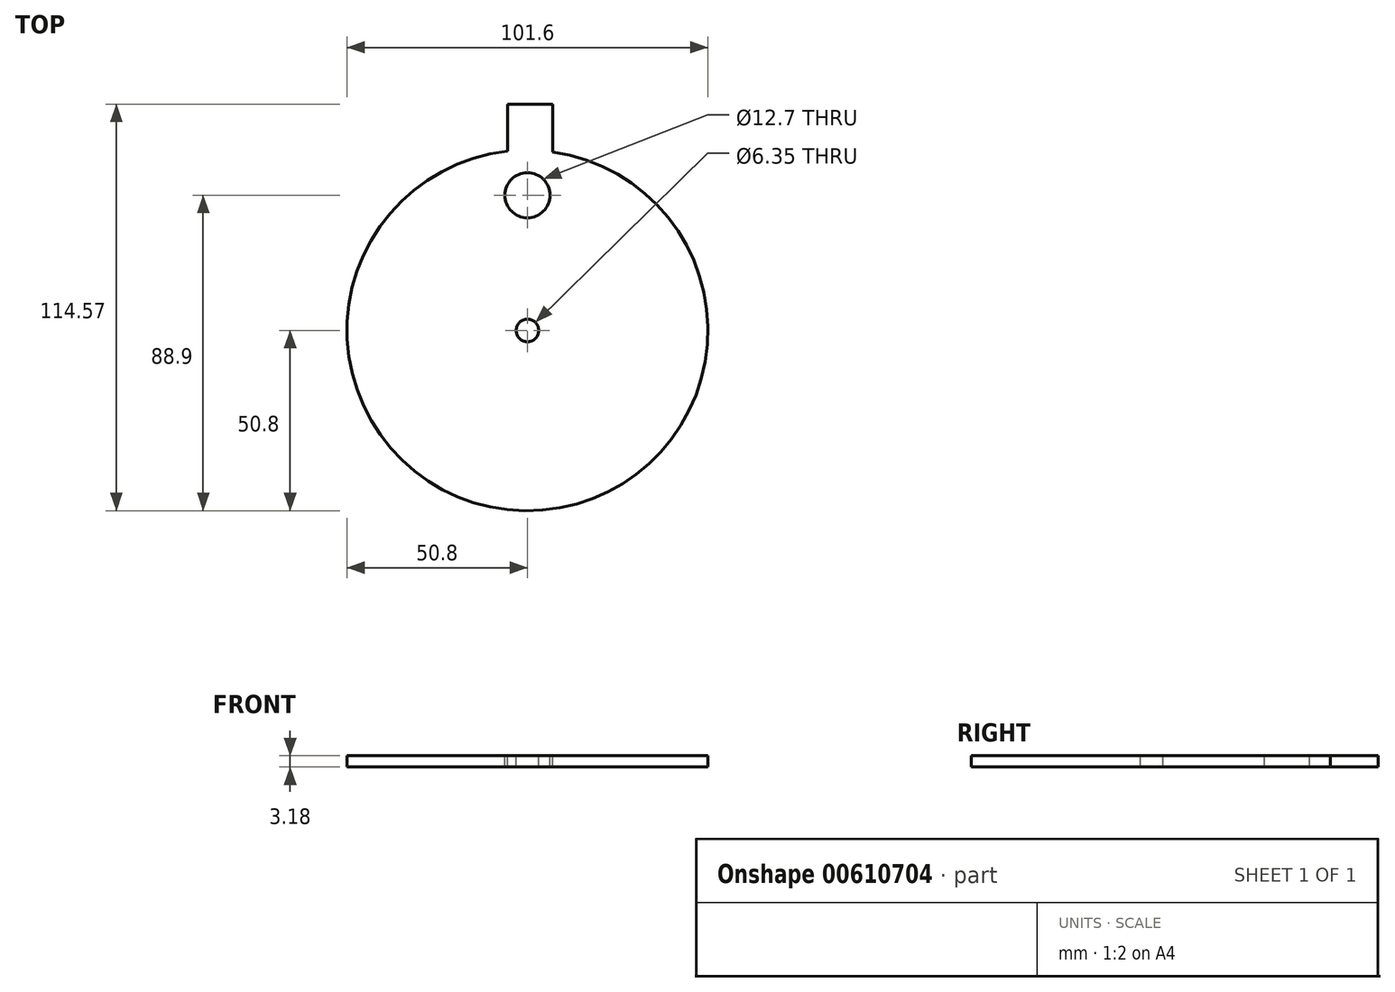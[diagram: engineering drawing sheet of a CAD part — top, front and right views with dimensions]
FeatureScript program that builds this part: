
annotation { "Feature Type Name" : "Feature", "Feature Type Description" : "" }
export const myFeature = defineFeature(function(context is Context, id is Id, definition is map)
    precondition{}
    {
        {
            var Q0;
            Q0=qCreatedBy(makeId("Top.planeOp"),FACE);
            var sketch = newSketch(context, id + "F0", { "sketchPlane" : qUnion([Q0])});
            skCircle(sketch, "E0", {"center": v(0, 0) * mm, "radius": 50.8 * mm});
            skSolve(sketch);
        }
        {
            var Q0;
            Q0=makeQuery(id+"F0.imprint","IMPRINT",FACE,{"disambiguationData":[TD([[makeQuery(id+"F0.imprint","IMPRINT",EDGE,{"derivedFrom":sQuery(id+"F0.wireOp",EDGE,"E0")}),1.0]])]});
            extrude(context, id + "F1", {"entities" : qUnion([Q0]), "depth" : 3.17 * mm, "offsetDistance" : 25.4 * mm});
        }
        {
            var Q0;
            Q0=makeQuery(id+"F1.opExtrude","CAP_FACE",FACE,{"disambiguationData":[OSD([sQuery(id+"F0.wireOp",EDGE,"E0")])],"isStart":false});
            var sketch = newSketch(context, id + "F2", { "sketchPlane" : qUnion([Q0])});
            skCircle(sketch, "E1", {"center": v(0, 38.1) * mm, "radius": 6.35 * mm});
            skSolve(sketch);
        }
        {
            var Q0;
            Q0=makeQuery(id+"F2.imprint","IMPRINT",FACE,{"disambiguationData":[TD([[makeQuery(id+"F2.imprint","IMPRINT",EDGE,{"derivedFrom":sQuery(id+"F2.wireOp",EDGE,"E1")}),1.0]])]});
            extrude(context, id + "F3", {"entities" : qUnion([Q0]), "operationType" : NewBodyOperationType.REMOVE, "depth" : -3.17 * mm, "offsetDistance" : 25.4 * mm});
        }
        {
            var Q0;
            Q0=makeQuery(id+"F2.imprint","IMPRINT",FACE,{"disambiguationData":[TD([[makeQuery(id+"F2.imprint","IMPRINT",EDGE,{"derivedFrom":sQuery(id+"F2.wireOp",EDGE,"E1")}),-1.0]])]});
            var sketch = newSketch(context, id + "F4", { "sketchPlane" : qUnion([Q0])});
            skCircle(sketch, "E2", {"center": v(0, 0) * mm, "radius": 3.18 * mm});
            skSolve(sketch);
        }
        {
            var Q0;
            Q0=makeQuery(id+"F4.imprint","IMPRINT",FACE,{"disambiguationData":[TD([[makeQuery(id+"F4.imprint","IMPRINT",EDGE,{"derivedFrom":sQuery(id+"F4.wireOp",EDGE,"E2")}),1.0]])]});
            extrude(context, id + "F5", {"entities" : qUnion([Q0]), "operationType" : NewBodyOperationType.REMOVE, "oppositeDirection" : true, "depth" : 25.4 * mm, "offsetDistance" : 25.4 * mm});
        }
        {
            var Q0;
            Q0=makeQuery(id+"F2.imprint","IMPRINT",FACE,{"disambiguationData":[TD([[makeQuery(id+"F2.imprint","IMPRINT",EDGE,{"derivedFrom":sQuery(id+"F2.wireOp",EDGE,"E1")}),-1.0]])]});
            var sketch = newSketch(context, id + "F6", { "sketchPlane" : qUnion([Q0])});
            skLineSegment(sketch, "E3", {"start": v(-5.63, 47.22) * mm, "end": v(-5.63, 63.77) * mm});
            skLineSegment(sketch, "E4", {"start": v(-5.63, 63.77) * mm, "end": v(7.07, 63.77) * mm});
            skLineSegment(sketch, "E5", {"start": v(7.07, 63.77) * mm, "end": v(7.07, 47.22) * mm});
            skLineSegment(sketch, "E6", {"start": v(-5.63, 47.22) * mm, "end": v(7.07, 47.22) * mm});
            skSolve(sketch);
        }
        {
            var Q0;
            {var subQ0=sQuery(id+"F6.wireOp",EDGE,"E4");Q0=makeQuery(id+"F6.imprint","IMPRINT",FACE,{"disambiguationData":[TD([[makeQuery(id+"F6.imprint","IMPRINT",EDGE,{"derivedFrom":subQ0}),-1.0]])]});}
            extrude(context, id + "F7", {"entities" : qUnion([Q0]), "operationType" : NewBodyOperationType.ADD, "oppositeDirection" : true, "depth" : 3.17 * mm, "offsetDistance" : 25.4 * mm});
        }
    });
